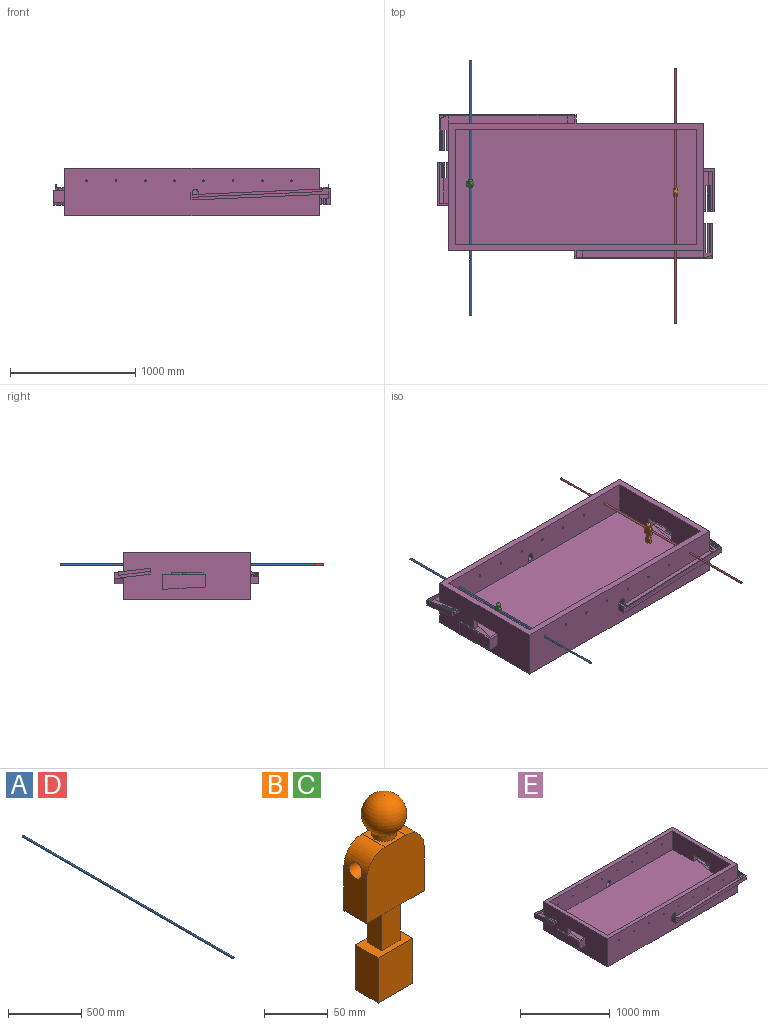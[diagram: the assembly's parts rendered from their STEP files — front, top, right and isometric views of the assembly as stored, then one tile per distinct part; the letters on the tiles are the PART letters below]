
ASSEMBLY  parts=5 mates=4
PART A: 3 faces, bbox 14.3x2032x14.3 mm
  f0: cylinder r=7.15mm len=2032mm, axis (0,1,0), area 91288.4mm2, adj f1,f2
  f1: plane 14.3x14.3mm, normal (0,-1,0), area 160.6mm2, adj f0
  f2: plane 14.3x14.3mm, normal (0,1,0), area 160.6mm2, adj f0
PART B: 21 faces, bbox 63.5x35.6x183.9 mm
  f0: cylinder r=9.53mm len=19.05mm, axis (0,0,1), area 304mm2, adj f1,f6
  f1: sphere r=17.78mm, area 3663.5mm2, adj f0
  f2: plane 43.18x25.4mm, normal (-1,0,0), area 1034.5mm2, adj f3,f7,f8,f9,f20
  f3: plane 63.5x25.4mm, normal (0,0,-1), area 1303.2mm2, adj f2,f4,f8,f9,f10,f11,f12,f13
  f4: plane 43.18x25.4mm, normal (1,0,0), area 1034.5mm2, adj f3,f5,f8,f9,f20
  f5: cylinder r=20.32mm len=25.4mm, axis (0,1,0), area 710.1mm2, adj f4,f6,f8,f9,f20
  f6: plane 25.4x22.86mm, normal (0,0,1), area 295.6mm2, adj f0,f5,f7,f8,f9
  f7: cylinder r=20.32mm len=25.4mm, axis (0,1,0), area 710mm2, adj f2,f6,f8,f9,f20
  f8: plane 63.5x63.5mm, normal (0,-1,0), area 3855mm2, adj f2,f3,f4,f5,f6,f7
  f9: plane 63.5x63.5mm, normal (0,1,0), area 3855mm2, adj f2,f3,f4,f5,f6,f7
  f10: plane 39.37x15.24mm, normal (-1,0,0), area 600mm2, adj f3,f12,f13,f14
  f11: plane 39.37x15.24mm, normal (1,0,0), area 600mm2, adj f3,f12,f13,f14
  f12: plane 39.37x20.32mm, normal (0,-1,0), area 800mm2, adj f3,f10,f11,f14
  f13: plane 39.37x20.32mm, normal (0,1,0), area 800mm2, adj f3,f10,f11,f14
  f14: plane 38.1x25.4mm, normal (0,0,1), area 658.1mm2, adj f10,f11,f12,f13,f15,f17,f18,f19
  f15: plane 43.18x25.4mm, normal (-1,0,0), area 1096.8mm2, adj f14,f16,f18,f19
  f16: plane 38.1x25.4mm, normal (0,0,-1), area 967.7mm2, adj f15,f17,f18,f19
  f17: plane 43.18x25.4mm, normal (1,0,0), area 1096.8mm2, adj f14,f16,f18,f19
  f18: plane 43.18x38.1mm, normal (0,-1,0), area 1645.2mm2, adj f14,f15,f16,f17
  f19: plane 43.18x38.1mm, normal (0,1,0), area 1645.2mm2, adj f14,f15,f16,f17
  f20: cylinder r=7.15mm len=63.5mm, axis (1,0,0), area 2808.4mm2, adj f2,f4,f5,f7
PART C: same geometry as B
PART D: same geometry as A
PART E: 147 faces, bbox 2209.8x1150.6x381 mm
  f0: plane 206.42x50.8mm, normal (1,0,0), area 4701.4mm2, adj f32,f33,f35,f37,f93,f145
  f1: plane 206.42x50.8mm, normal (-1,0,0), area 5112.7mm2, adj f33,f86,f89,f90,f93,f145
  f2: plane 206.42x50.8mm, normal (1,0,0), area 5112.7mm2, adj f31,f33,f34,f36,f94,f146
  f3: plane 206.42x50.8mm, normal (-1,0,0), area 4701.4mm2, adj f32,f33,f35,f37,f94,f146
  f4: plane 1071.88x381mm, normal (1,0,0), area 347609.5mm2, adj f27,f28,f29,f31,f33,f34,f36,f42
  f5: plane 1024.44x66.55mm, normal (0,-1,0), area 21852mm2, adj f6,f12,f109,f110,f113,f114,f138
  f6: plane 1076.96x48.6mm, normal (0.05,0,1), area 8008.4mm2, adj f5,f110,f116,f118,f119,f138,f139
  f7: plane 257.51x56.09mm, normal (1,0,0), area 6412.3mm2, adj f12,f14,f117,f138
  f8: plane 119.38x50.8mm, normal (1,0,0), area 2992.5mm2, adj f17,f18,f20,f22,f127,f137
  f9: plane 119.38x50.8mm, normal (-1,0,0), area 3193.7mm2, adj f18,f120,f123,f124,f127,f137
  f10: plane 119.38x50.8mm, normal (1,0,0), area 3193.7mm2, adj f16,f18,f19,f21,f128,f136
  f11: plane 119.38x50.8mm, normal (-1,0,0), area 2992.5mm2, adj f17,f18,f20,f22,f128,f136
  f12: plane 279.4x68.58mm, normal (0,0.13,0.99), area 14528.9mm2, adj f5,f7,f14,f15,f23,f103,f104,f129
  f13: plane 279.4x76.2mm, normal (0,-0.13,-0.99), area 17320.3mm2, adj f14,f15,f23,f104,f105,f115,f129,f130
  f14: plane 46.6x16.51mm, normal (0,-1,0), area 558.3mm2, adj f7,f12,f13,f105,f117,f133
  f15: plane 22.86x16.51mm, normal (0,-1,0), area 377.4mm2, adj f12,f13,f130,f134
  f16: plane 119x29.21mm, normal (0,1,0), area 2350mm2, adj f10,f18,f21,f122,f125,f126
  f17: plane 50.8x16.51mm, normal (0,1,0), area 838.7mm2, adj f8,f11,f18,f22
  f18: plane 342.9x88.9mm, normal (0,-0.05,-1), area 27491.5mm2, adj f8,f9,f10,f11,f16,f17,f23,f120
  f19: plane 27.21x17.78mm, normal (0,-1,0), area 428.2mm2, adj f10,f21,f125,f135,f136
  f20: plane 30.48x16.51mm, normal (0,-1,0), area 492.6mm2, adj f8,f11,f22,f136,f137
  f21: plane 17.78x16.51mm, normal (0,0,1), area 293.5mm2, adj f10,f16,f19,f125
  f22: plane 17.78x16.51mm, normal (0,0,1), area 293.5mm2, adj f8,f11,f17,f20
  f23: plane 1079.5x381mm, normal (-1,0,0), area 347533.6mm2, adj f12,f13,f18,f42,f43,f44,f45,f51
  f24: plane 249.41x53.97mm, normal (-1,0,0), area 5601.9mm2, adj f27,f74,f84,f101
  f25: plane 1041.48x65.04mm, normal (0,1,0), area 21177.2mm2, adj f26,f27,f38,f39,f40,f41,f77,f101
  f26: plane 1092.2x46.42mm, normal (-0.04,0,1), area 8200.9mm2, adj f25,f73,f75,f77,f84,f85,f101,f102
  f27: plane 271.78x71.12mm, normal (0,-0.13,0.99), area 12856.4mm2, adj f4,f24,f25,f29,f30,f38,f74,f95
  f28: plane 271.78x76.2mm, normal (0,0.13,-0.99), area 14893.3mm2, adj f4,f29,f30,f74,f75,f82,f95,f96
  f29: plane 22.86x17.78mm, normal (0,1,0), area 406.5mm2, adj f4,f27,f28,f99
  f30: plane 22.86x16.51mm, normal (0,1,0), area 377.4mm2, adj f27,f28,f96,f100
  f31: plane 50.8x17.78mm, normal (0,-1,0), area 903.2mm2, adj f2,f4,f33,f36
  f32: plane 50.8x16.51mm, normal (0,-1,0), area 838.7mm2, adj f0,f3,f33,f37
  f33: plane 342.9x88.9mm, normal (0,0.04,-1), area 25260.3mm2, adj f0,f1,f2,f3,f4,f31,f32,f86
  f34: plane 27.75x17.78mm, normal (0,1,0), area 466.3mm2, adj f2,f4,f36,f146
  f35: plane 31.35x16.51mm, normal (0,1,0), area 505.9mm2, adj f0,f3,f37,f145,f146
  f36: plane 17.78x17.78mm, normal (0,0,1), area 316.1mm2, adj f2,f4,f31,f34
  f37: plane 17.78x16.51mm, normal (0,0,1), area 293.5mm2, adj f0,f3,f32,f35
  f38: plane 55.88x8.08mm, normal (-1,0,0), area 252.9mm2, adj f25,f27,f39,f43
  f39: plane 965.2x55.88mm, normal (-0.04,0,1), area 53984.1mm2, adj f25,f38,f41,f43
  f40: plane 106.68x50.8mm, normal (0,0.06,1), area 5429mm2, adj f25,f41,f48,f77
  f41: plane 106.68x43.68mm, normal (-1,0,0), area 2304.1mm2, adj f25,f39,f40,f43,f48,f81
  f42: plane 2032x1016mm, normal (0,0,1), area 299354.2mm2, adj f4,f23,f43,f44,f46,f47,f48,f49
  f43: plane 2032x381mm, normal (0,-1,0), area 745886.4mm2, adj f4,f23,f38,f39,f41,f42,f45,f57
  f44: plane 2032x381mm, normal (0,1,0), area 746235.7mm2, adj f4,f23,f42,f45,f65,f66,f67,f68
  f45: plane 2032x1016mm, normal (0,0,-1), area 2064512mm2, adj f4,f23,f43,f44
  f46: plane 1930.4x254mm, normal (0,-1,0), area 485960.6mm2, adj f42,f47,f49,f50,f65,f66,f67,f68
  f47: plane 914.4x254mm, normal (1,0,0), area 209677mm2, adj f42,f46,f48,f50,f51,f52,f53
  f48: plane 1930.4x254mm, normal (0,1,0), area 485960.6mm2, adj f40,f41,f42,f47,f49,f50,f57,f58
  f49: plane 914.4x254mm, normal (-1,0,0), area 209677mm2, adj f42,f46,f48,f50,f54,f55,f56
  f50: plane 2032x914.4mm, normal (0,0,1), area 1778061mm2, adj f46,f47,f48,f49,f51,f55,f140,f142
  f51: plane 128.27x94.94mm, normal (0,1,0), area 10556.5mm2, adj f23,f47,f50,f53,f122,f125,f135,f136
  f52: plane 101.6x50.8mm, normal (0,-1,0), area 4838.7mm2, adj f23,f47,f53,f140
  f53: plane 254x50.8mm, normal (0,0,-1), area 12903.2mm2, adj f23,f47,f51,f52
  f54: plane 99.06x50.8mm, normal (0,1,0), area 4774.2mm2, adj f4,f49,f56,f141,f142
  f55: plane 128.27x95.55mm, normal (0,-1,0), area 11547.9mm2, adj f49,f50,f56,f88,f92,f144,f145,f146
  f56: plane 254x50.8mm, normal (0,0,-1), area 12903.2mm2, adj f4,f49,f54,f55
  f57: cylinder r=7.14mm len=50.8mm, axis (0,-1,0), area 2280.2mm2, adj f43,f48
  f58: cylinder r=7.14mm len=50.8mm, axis (0,-1,0), area 2280.2mm2, adj f43,f48
  f59: cylinder r=7.14mm len=50.8mm, axis (0,-1,0), area 2280.2mm2, adj f43,f48
  f60: cylinder r=7.14mm len=50.8mm, axis (0,-1,0), area 2280.2mm2, adj f43,f48
  f61: cylinder r=7.14mm len=50.8mm, axis (0,-1,0), area 2280.2mm2, adj f43,f48
  f62: cylinder r=7.14mm len=50.8mm, axis (0,-1,0), area 2280.2mm2, adj f43,f48
  f63: cylinder r=7.14mm len=50.8mm, axis (0,-1,0), area 2280.2mm2, adj f43,f48
  f64: cylinder r=7.14mm len=50.8mm, axis (0,-1,0), area 2280.2mm2, adj f43,f48
  f65: cylinder r=7.14mm len=50.8mm, axis (0,-1,0), area 2280.2mm2, adj f44,f46
  f66: cylinder r=7.14mm len=50.8mm, axis (0,-1,0), area 2280.2mm2, adj f44,f46
  f67: cylinder r=7.14mm len=50.8mm, axis (0,-1,0), area 2280.2mm2, adj f44,f46
  f68: cylinder r=7.14mm len=50.8mm, axis (0,-1,0), area 2280.2mm2, adj f44,f46
  f69: cylinder r=7.14mm len=50.8mm, axis (0,-1,0), area 2280.2mm2, adj f44,f46
  f70: cylinder r=7.14mm len=50.8mm, axis (0,-1,0), area 2280.2mm2, adj f44,f46
  f71: cylinder r=7.14mm len=50.8mm, axis (0,-1,0), area 2280.2mm2, adj f44,f46
  f72: cylinder r=7.14mm len=50.8mm, axis (0,-1,0), area 2280.2mm2, adj f44,f46
  f73: plane 1107.44x89.6mm, normal (0,-1,0), area 48252.3mm2, adj f26,f75,f76,f77,f78,f79,f80,f83
  f74: plane 45.45x16.51mm, normal (0,1,0), area 492.2mm2, adj f24,f27,f28,f75,f84,f97
  f75: plane 279.4x81.01mm, normal (1,0,0), area 12705.8mm2, adj f26,f28,f73,f74,f82,f83,f84
  f76: plane 1016x63.5mm, normal (0.04,0,-1), area 64574.2mm2, adj f4,f43,f73,f80,f83
  f77: plane 114.3x47.48mm, normal (1,0,0), area 4609.3mm2, adj f25,f26,f40,f43,f48,f73,f78,f81
  f78: plane 63.5x15.24mm, normal (0,0,1), area 967.7mm2, adj f43,f73,f77,f79
  f79: plane 63.5x63.5mm, normal (-1,0,0), area 4032.3mm2, adj f43,f73,f78,f80
  f80: plane 63.5x15.24mm, normal (0,0,-1), area 967.7mm2, adj f43,f73,f76,f79
  f81: bspline ~60.96x54.45mm, area 4057.3mm2, adj f41,f43,f48,f77
  f82: plane 76.2x0.97mm, normal (0,1,0), area 73.9mm2, adj f4,f28,f75,f83
  f83: plane 76.2x7.62mm, normal (0,0,-1), area 580.6mm2, adj f73,f75,f76,f82
  f84: plane 274.61x34.95mm, normal (0,-0.13,0.99), area 1473.1mm2, adj f24,f26,f74,f75,f85,f101,f102,f143
  f85: plane 5.08x0.22mm, normal (0,-1,0), area 0.5mm2, adj f26,f84,f102
  f86: plane 127x29.21mm, normal (0,-1,0), area 2451.6mm2, adj f1,f33,f88,f90,f91,f92
  f87: plane 113.5x88.9mm, normal (0,1,0), area 10090.1mm2, adj f4,f33,f88,f91
  f88: plane 342.9x88.9mm, normal (0,0,1), area 5903.2mm2, adj f4,f55,f86,f87,f91,f92
  f89: plane 27.75x17.78mm, normal (0,1,0), area 434.9mm2, adj f1,f90,f92,f144,f145
  f90: plane 17.78x16.51mm, normal (0,0,1), area 293.5mm2, adj f1,f86,f89,f92
  f91: plane 342.9x127mm, normal (1,0,0), area 41233.7mm2, adj f33,f86,f87,f88
  f92: plane 322.58x100.9mm, normal (-1,0,0), area 30280.4mm2, adj f55,f86,f88,f89,f90,f144
  f93: plane 22.35x12.7mm, normal (0,-1,0), area 270mm2, adj f0,f1,f33,f145
  f94: plane 22.35x12.7mm, normal (0,-1,0), area 270mm2, adj f2,f3,f33,f146
  f95: plane 22.86x12.7mm, normal (0,1,0), area 290.3mm2, adj f27,f28,f96,f97
  f96: plane 233.68x52.6mm, normal (1,0,0), area 5341.9mm2, adj f27,f28,f30,f95
  f97: plane 233.68x52.6mm, normal (-1,0,0), area 5341.9mm2, adj f27,f28,f74,f95
  f98: plane 22.86x12.7mm, normal (0,1,0), area 290.3mm2, adj f27,f28,f99,f100
  f99: plane 233.68x52.6mm, normal (1,0,0), area 5341.9mm2, adj f27,f28,f29,f98
  f100: plane 233.68x52.6mm, normal (-1,0,0), area 5341.9mm2, adj f27,f28,f30,f98
  f101: plane 50.8x27.77mm, normal (-0.45,0.89,0.11), area 1160.1mm2, adj f24,f25,f26,f27,f84,f143
  f102: plane 1.7x0.22mm, normal (1,0,0), area 0.2mm2, adj f26,f84,f85
  f103: plane 63.5x8.08mm, normal (1,0,0), area 256.6mm2, adj f12,f44,f109
  f104: plane 22.86x17.78mm, normal (0,-1,0), area 406.5mm2, adj f12,f13,f23,f131
  f105: plane 287.02x82.16mm, normal (-1,0,0), area 13797.1mm2, adj f13,f14,f115,f116,f117
  f106: plane 71.12x63.5mm, normal (1,0,0), area 4516.1mm2, adj f44,f107,f111,f116
  f107: plane 71.12x15.24mm, normal (0,0,-1), area 1083.9mm2, adj f44,f106,f108,f116
  f108: plane 1000.76x71.12mm, normal (-0.04,0,-1), area 71240.3mm2, adj f23,f44,f107,f115,f116
  f109: plane 949.96x63.5mm, normal (0.04,0,1), area 60378.6mm2, adj f5,f44,f103,f113
  f110: plane 121.92x47.48mm, normal (-1,0,0), area 4920.7mm2, adj f5,f6,f44,f46,f111,f112,f114,f116
  f111: plane 71.12x15.24mm, normal (0,0,1), area 1083.9mm2, adj f44,f106,f110,f116
  f112: bspline ~60.96x54.45mm, area 4057.3mm2, adj f44,f46,f110,f113
  f113: plane 114.3x43.68mm, normal (1,0,0), area 2324.4mm2, adj f5,f44,f46,f109,f112,f114
  f114: plane 114.3x50.8mm, normal (0,-0.06,1), area 5816.8mm2, adj f5,f46,f110,f113
  f115: plane 76.2x7.62mm, normal (0,0,-1), area 580.6mm2, adj f13,f105,f108,f116
  f116: plane 1092.2x91.78mm, normal (0,1,0), area 48741.7mm2, adj f6,f105,f106,f107,f108,f110,f111,f115
  f117: plane 287.02x58.42mm, normal (0,0.12,0.99), area 2847.2mm2, adj f7,f14,f105,f118,f119,f138,f139
  f118: plane 7.62x0.34mm, normal (0,1,0), area 1.3mm2, adj f6,f117,f119
  f119: plane 4.39x0.84mm, normal (1,0,0), area 2.6mm2, adj f6,f117,f118,f139
  f120: plane 50.8x17.78mm, normal (0,1,0), area 903.2mm2, adj f9,f18,f23,f124
  f121: plane 100.5x88.9mm, normal (0,-1,0), area 8934.8mm2, adj f18,f23,f122,f126
  f122: plane 342.9x88.9mm, normal (0,0,1), area 5903.2mm2, adj f16,f23,f51,f121,f125,f126
  f123: plane 27.21x17.78mm, normal (0,-1,0), area 459.2mm2, adj f9,f23,f124,f137
  f124: plane 17.78x17.78mm, normal (0,0,1), area 316.1mm2, adj f9,f23,f120,f123
  f125: plane 322.58x92.64mm, normal (1,0,0), area 26943.6mm2, adj f16,f19,f21,f51,f122,f135
  f126: plane 342.9x119mm, normal (-1,0,0), area 37633.6mm2, adj f16,f18,f121,f122
  f127: plane 22.63x12.7mm, normal (0,1,0), area 274.8mm2, adj f8,f9,f18,f137
  f128: plane 22.63x12.7mm, normal (0,1,0), area 274.8mm2, adj f10,f11,f18,f136
  f129: plane 22.86x12.7mm, normal (0,-1,0), area 290.3mm2, adj f12,f13,f130,f131
  f130: plane 161.76x43.45mm, normal (1,0,0), area 3697.7mm2, adj f12,f13,f15,f129
  f131: plane 161.76x43.45mm, normal (-1,0,0), area 3697.7mm2, adj f12,f13,f104,f129
  f132: plane 22.86x12.7mm, normal (0,-1,0), area 290.3mm2, adj f12,f13,f133,f134
  f133: plane 161.76x43.45mm, normal (1,0,0), area 3697.7mm2, adj f12,f13,f14,f132
  f134: plane 161.76x43.45mm, normal (-1,0,0), area 3697.7mm2, adj f12,f13,f15,f132
  f135: plane 304.8x16.44mm, normal (0,-0.05,-1), area 387.7mm2, adj f19,f51,f125,f136
  f136: plane 304.8x38.74mm, normal (0.15,0.05,0.99), area 10658.2mm2, adj f10,f11,f19,f20,f51,f128,f135,f137
  f137: plane 304.8x38.74mm, normal (-0.15,0.05,0.99), area 10658.2mm2, adj f8,f9,f20,f23,f51,f123,f127,f136
  f138: plane 50.8x29.19mm, normal (0.45,-0.89,0.11), area 1418mm2, adj f5,f6,f7,f12,f117,f139
  f139: plane 50.8x3.14mm, normal (0,0.99,-0.13), area 101.9mm2, adj f6,f117,f119,f138
  f140: plane 254x50.8mm, normal (-0.24,0.05,0.97), area 6658mm2, adj f23,f50,f52
  f141: plane 254x10.16mm, normal (-1,0,0), area 20.3mm2, adj f54,f142,f146
  f142: plane 254x50.8mm, normal (0.2,-0.04,0.98), area 6584.4mm2, adj f50,f54,f141
  f143: plane 47.41x23.51mm, normal (-0.04,-0.13,0.99), area 562.4mm2, adj f26,f84,f101
  f144: plane 304.8x12mm, normal (0,0.04,-1), area 387.4mm2, adj f55,f89,f92,f145
  f145: plane 304.8x38.74mm, normal (-0.17,-0.04,0.98), area 9555.5mm2, adj f0,f1,f35,f55,f89,f93,f144,f146
  f146: plane 304.8x38.74mm, normal (0.17,-0.04,0.98), area 9555.5mm2, adj f2,f3,f4,f34,f35,f55,f94,f141
PLACE A rot(axis=(0,1,0),10.6deg) t=(175.26,1518.11,279.4)mm
PLACE B rot(axis=(0,0,1),90deg) t=(1811.02,467.6,279.4)mm
PLACE C rot(axis=(0.09,0.09,0.99),90.5deg) t=(175.26,533.86,279.4)mm
PLACE D rot(axis=(0,1,0),0.2deg) t=(1811.02,1451.85,279.4)mm
PLACE E at identity fixed
MATE cylindrical D.f0 <-> E.f63  axis (0,1,0) through (1811.02,-580.15,279.4)mm
MATE fastened B.f20 <-> D.f0  axis (0,1,0) through (1811.02,435.85,279.4)mm
MATE cylindrical A.f0 <-> E.f61  axis (0,1,0) through (175.26,-513.89,279.4)mm
MATE fastened C.f20 <-> A.f0  axis (0,1,0) through (175.26,502.11,279.4)mm
